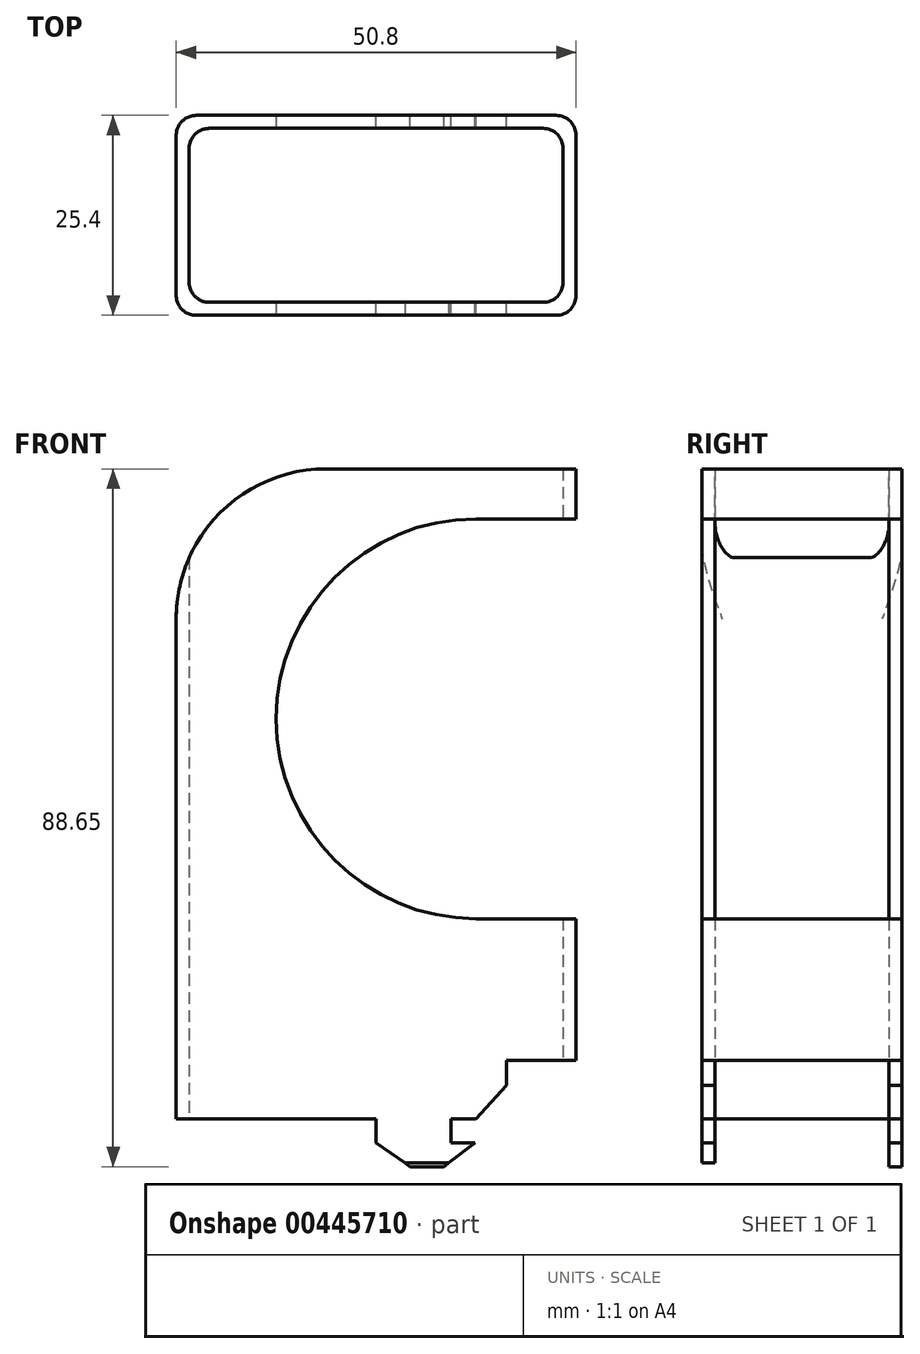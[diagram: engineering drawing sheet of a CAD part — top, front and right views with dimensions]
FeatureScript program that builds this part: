
annotation { "Feature Type Name" : "Feature", "Feature Type Description" : "" }
export const myFeature = defineFeature(function(context is Context, id is Id, definition is map)
    precondition{}
    {
        {
            var Q0;
            Q0=qCreatedBy(makeId("Top.planeOp"),FACE);
            var sketch = newSketch(context, id + "F0", { "sketchPlane" : qUnion([Q0])});
            skLineSegment(sketch, "E0.bottom", {"start": v(2.54, 0) * mm, "end": v(48.26, 0) * mm});
            skLineSegment(sketch, "E0.top", {"start": v(2.54, 25.4) * mm, "end": v(48.26, 25.4) * mm});
            skLineSegment(sketch, "E0.left", {"start": v(0, 2.54) * mm, "end": v(0, 22.86) * mm});
            skLineSegment(sketch, "E0.right", {"start": v(50.8, 2.54) * mm, "end": v(50.8, 22.86) * mm});
            skPoint(sketch, "E1.visualSharp", {"position": v(0, 25.4) * mm});
            skArc(sketch, "E1.filletArc", {"start": v(2.54, 25.4) * mm, "mid": v(0.74, 24.66) * mm, "end": v(0, 22.86) * mm});
            skPoint(sketch, "E2.visualSharp", {"position": v(50.8, 25.4) * mm});
            skArc(sketch, "E2.filletArc", {"start": v(50.8, 22.86) * mm, "mid": v(50.06, 24.66) * mm, "end": v(48.26, 25.4) * mm});
            skPoint(sketch, "E3.visualSharp", {"position": v(50.8, 0) * mm});
            skArc(sketch, "E3.filletArc", {"start": v(48.26, 0) * mm, "mid": v(50.06, 0.74) * mm, "end": v(50.8, 2.54) * mm});
            skPoint(sketch, "E4.visualSharp", {"position": v(0, 0) * mm});
            skArc(sketch, "E4.filletArc", {"start": v(0, 2.54) * mm, "mid": v(0.74, 0.74) * mm, "end": v(2.54, 0) * mm});
            skLineSegment(sketch, "E5.0", {"start": v(4.2, 23.75) * mm, "end": v(46.6, 23.75) * mm});
            skLineSegment(sketch, "E5.1", {"start": v(1.65, 4.2) * mm, "end": v(1.65, 21.2) * mm});
            skLineSegment(sketch, "E5.2", {"start": v(4.2, 1.65) * mm, "end": v(46.6, 1.65) * mm});
            skLineSegment(sketch, "E5.3", {"start": v(49.15, 4.2) * mm, "end": v(49.15, 21.2) * mm});
            skPoint(sketch, "E6.visualSharp", {"position": v(1.65, 23.75) * mm});
            skArc(sketch, "E6.filletArc", {"start": v(4.2, 23.75) * mm, "mid": v(2.4, 23) * mm, "end": v(1.65, 21.2) * mm});
            skPoint(sketch, "E7.visualSharp", {"position": v(1.65, 1.65) * mm});
            skArc(sketch, "E7.filletArc", {"start": v(1.65, 4.2) * mm, "mid": v(2.4, 2.4) * mm, "end": v(4.2, 1.65) * mm});
            skPoint(sketch, "E8.visualSharp", {"position": v(49.15, 23.75) * mm});
            skArc(sketch, "E8.filletArc", {"start": v(49.15, 21.2) * mm, "mid": v(48.4, 23) * mm, "end": v(46.6, 23.75) * mm});
            skPoint(sketch, "E9.visualSharp", {"position": v(49.15, 1.65) * mm});
            skArc(sketch, "E9.filletArc", {"start": v(46.6, 1.65) * mm, "mid": v(48.4, 2.4) * mm, "end": v(49.15, 4.2) * mm});
            skSolve(sketch);
        }
        {
            var Q0;
            Q0=makeQuery(id+"F0.imprint","IMPRINT",FACE,{"disambiguationData":[TD([[makeQuery(id+"F0.imprint","IMPRINT",EDGE,{"derivedFrom":sQuery(id+"F0.wireOp",EDGE,"E0.bottom")}),1.0]])]});
            extrude(context, id + "F1", {"entities" : qUnion([Q0]), "depth" : 82.55 * mm});
        }
        {
            var Q0;
            Q0=makeQuery(id+"F1.opExtrude","CAP_FACE",FACE,{"disambiguationData":[OSD([sQuery(id+"F0.wireOp",EDGE,"E0.bottom"),sQuery(id+"F0.wireOp",EDGE,"E0.top"),sQuery(id+"F0.wireOp",EDGE,"E0.left"),sQuery(id+"F0.wireOp",EDGE,"E0.right"),sQuery(id+"F0.wireOp",EDGE,"E1.filletArc"),sQuery(id+"F0.wireOp",EDGE,"E2.filletArc"),sQuery(id+"F0.wireOp",EDGE,"E3.filletArc"),sQuery(id+"F0.wireOp",EDGE,"E4.filletArc"),sQuery(id+"F0.wireOp",EDGE,"E5.0"),sQuery(id+"F0.wireOp",EDGE,"E5.1"),sQuery(id+"F0.wireOp",EDGE,"E5.2"),sQuery(id+"F0.wireOp",EDGE,"E5.3"),sQuery(id+"F0.wireOp",EDGE,"E6.filletArc"),sQuery(id+"F0.wireOp",EDGE,"E7.filletArc"),sQuery(id+"F0.wireOp",EDGE,"E8.filletArc"),sQuery(id+"F0.wireOp",EDGE,"E9.filletArc")])],"isStart":true});
            var sketch = newSketch(context, id + "F2", { "sketchPlane" : qUnion([Q0])});
            skLineSegment(sketch, "E10", {"start": v(34.93, 0) * mm, "end": v(34.93, -1.65) * mm});
            skLineSegment(sketch, "E11", {"start": v(25.4, 0) * mm, "end": v(25.4, -1.65) * mm});
            skLineSegment(sketch, "E12", {"start": v(34.92, -23.75) * mm, "end": v(34.92, -25.4) * mm});
            skLineSegment(sketch, "E13", {"start": v(25.4, -23.75) * mm, "end": v(25.4, -25.4) * mm});
            skSolve(sketch);
        }
        {
            var Q0;
            Q0 = qSketchRegion(id + "F2", true);
            var Q1;
            {var subQ0=sQuery(id+"F2.wireOp",EDGE,"E10");Q1=makeQuery(id+"F2.imprint","IMPRINT",FACE,{"disambiguationData":[TD([[makeQuery(id+"F2.imprint","IMPRINT",EDGE,{"derivedFrom":subQ0}),-1.0]])]});}
            var Q2;
            {var subQ0=sQuery(id+"F2.wireOp",EDGE,"E12");Q2=makeQuery(id+"F2.imprint","IMPRINT",FACE,{"disambiguationData":[TD([[makeQuery(id+"F2.imprint","IMPRINT",EDGE,{"derivedFrom":subQ0}),-1.0]])]});}
            extrude(context, id + "F3", {"entities" : qUnion([Q0, Q1, Q2]), "operationType" : NewBodyOperationType.ADD, "depth" : 12.7 * mm});
        }
        {
            var Q0;
            Q0=makeQuery(id+"F3.opExtrude","SWEPT_FACE",FACE,{"disambiguationData":[OSD([sQuery(id+"F2.wireOp",EDGE,"E10")])]});
            var sketch = newSketch(context, id + "F4", { "sketchPlane" : qUnion([Q0])});
            skLineSegment(sketch, "E14", {"start": v(0, -3.05) * mm, "end": v(1.65, -3.05) * mm});
            skSolve(sketch);
        }
        {
            var Q0;
            {var subQ0=sQuery(id+"F4.wireOp",EDGE,"E14");Q0=makeQuery(id+"F4.imprint","IMPRINT",FACE,{"disambiguationData":[TD([[makeQuery(id+"F4.imprint","IMPRINT",EDGE,{"derivedFrom":subQ0}),-1.0]])]});}
            extrude(context, id + "F5", {"entities" : qUnion([Q0]), "operationType" : NewBodyOperationType.ADD, "depth" : 3.05 * mm});
        }
        {
            var Q0;
            Q0=makeQuery(id+"F3.opExtrude","SWEPT_FACE",FACE,{"disambiguationData":[OSD([sQuery(id+"F2.wireOp",EDGE,"E12")])]});
            var sketch = newSketch(context, id + "F6", { "sketchPlane" : qUnion([Q0])});
            skLineSegment(sketch, "E15", {"start": v(23.75, -3.05) * mm, "end": v(25.4, -3.05) * mm});
            skSolve(sketch);
        }
        {
            var Q0;
            Q0 = qSketchRegion(id + "F6", true);
            var Q1;
            {var subQ0=sQuery(id+"F6.wireOp",EDGE,"E15");Q1=makeQuery(id+"F6.imprint","IMPRINT",FACE,{"disambiguationData":[TD([[makeQuery(id+"F6.imprint","IMPRINT",EDGE,{"derivedFrom":subQ0}),-1.0]])]});}
            extrude(context, id + "F7", {"entities" : qUnion([Q0, Q1]), "operationType" : NewBodyOperationType.ADD, "depth" : 3.05 * mm});
        }
        {
            var Q0;
            {var subQ0=sQuery(id+"F0.wireOp",EDGE,"E0.bottom");Q0=makeQuery(id+"F5.boolean.opBoolean","MERGE",FACE,{"derivedFrom":[makeQuery(id+"F3.boolean.opBoolean","MERGE",FACE,{"derivedFrom":[makeQuery(id+"F1.opExtrude","SWEPT_FACE",FACE,{"disambiguationData":[OSD([subQ0])]}),makeQuery(id+"F3.opExtrude","SWEPT_FACE",FACE,{"disambiguationData":[OSD([subQ0])]})]}),makeQuery(id+"F5.opExtrude","SWEPT_FACE",FACE,{"disambiguationData":[OSD([subQ0,sQuery(id+"F2.wireOp",EDGE,"E10")])]})]});}
            var sketch = newSketch(context, id + "F8", { "sketchPlane" : qUnion([Q0])});
            skLineSegment(sketch, "E16", {"start": v(37.97, -3.05) * mm, "end": v(25.4, -12.7) * mm});
            skSolve(sketch);
        }
        {
            var Q0;
            Q0 = qSketchRegion(id + "F8", true);
            var Q1;
            Q1=makeQuery(id+"F8.imprint","IMPRINT",FACE,{"disambiguationData":[TD([[makeQuery(id+"F8.imprint","IMPRINT",EDGE,{"derivedFrom":sQuery(id+"F8.wireOp",EDGE,"E16")}),1.0]])]});
            extrude(context, id + "F9", {"entities" : qUnion([Q0, Q1]), "operationType" : NewBodyOperationType.REMOVE, "oppositeDirection" : true, "depth" : 6.35 * mm});
        }
        {
            var Q0;
            {var subQ0=sQuery(id+"F0.wireOp",EDGE,"E0.top");Q0=makeQuery(id+"F7.boolean.opBoolean","MERGE",FACE,{"derivedFrom":[makeQuery(id+"F3.boolean.opBoolean","MERGE",FACE,{"derivedFrom":[makeQuery(id+"F1.opExtrude","SWEPT_FACE",FACE,{"disambiguationData":[OSD([subQ0])]}),makeQuery(id+"F3.opExtrude","SWEPT_FACE",FACE,{"disambiguationData":[OSD([subQ0])]})]}),makeQuery(id+"F7.opExtrude","SWEPT_FACE",FACE,{"disambiguationData":[OSD([subQ0,sQuery(id+"F2.wireOp",EDGE,"E12")])]})]});}
            var sketch = newSketch(context, id + "F10", { "sketchPlane" : qUnion([Q0])});
            skLineSegment(sketch, "E17", {"start": v(-37.97, -3.05) * mm, "end": v(-25.4, -12.7) * mm});
            skSolve(sketch);
        }
        {
            var Q0;
            Q0 = qSketchRegion(id + "F10", true);
            var Q1;
            Q1=makeQuery(id+"F10.imprint","IMPRINT",FACE,{"disambiguationData":[TD([[makeQuery(id+"F10.imprint","IMPRINT",EDGE,{"derivedFrom":sQuery(id+"F10.wireOp",EDGE,"E17")}),-1.0]])]});
            extrude(context, id + "F11", {"entities" : qUnion([Q0, Q1]), "operationType" : NewBodyOperationType.REMOVE, "oppositeDirection" : true, "depth" : 6.35 * mm});
        }
        {
            var Q0;
            {var subQ0=sQuery(id+"F0.wireOp",EDGE,"E0.top");Q0=makeQuery(id+"F7.boolean.opBoolean","MERGE",FACE,{"derivedFrom":[makeQuery(id+"F3.boolean.opBoolean","MERGE",FACE,{"derivedFrom":[makeQuery(id+"F1.opExtrude","SWEPT_FACE",FACE,{"disambiguationData":[OSD([subQ0])]}),makeQuery(id+"F3.opExtrude","SWEPT_FACE",FACE,{"disambiguationData":[OSD([subQ0])]})]}),makeQuery(id+"F7.opExtrude","SWEPT_FACE",FACE,{"disambiguationData":[OSD([subQ0,sQuery(id+"F2.wireOp",EDGE,"E12")])]})]});}
            var sketch = newSketch(context, id + "F12", { "sketchPlane" : qUnion([Q0])});
            skLineSegment(sketch, "E18", {"start": v(-34, -6.1) * mm, "end": v(-25.4, -6.1) * mm});
            skSolve(sketch);
        }
        {
            var Q0;
            {var subQ0=sQuery(id+"F12.wireOp",EDGE,"E18");Q0=makeQuery(id+"F12.imprint","IMPRINT",FACE,{"disambiguationData":[TD([[makeQuery(id+"F12.imprint","IMPRINT",EDGE,{"derivedFrom":subQ0}),-1.0]])]});}
            extrude(context, id + "F13", {"entities" : qUnion([Q0]), "operationType" : NewBodyOperationType.REMOVE, "oppositeDirection" : true, "depth" : 3.17 * mm});
        }
        {
            var Q0;
            {var subQ0=sQuery(id+"F0.wireOp",EDGE,"E0.bottom");Q0=makeQuery(id+"F5.boolean.opBoolean","MERGE",FACE,{"derivedFrom":[makeQuery(id+"F3.boolean.opBoolean","MERGE",FACE,{"derivedFrom":[makeQuery(id+"F1.opExtrude","SWEPT_FACE",FACE,{"disambiguationData":[OSD([subQ0])]}),makeQuery(id+"F3.opExtrude","SWEPT_FACE",FACE,{"disambiguationData":[OSD([subQ0])]})]}),makeQuery(id+"F5.opExtrude","SWEPT_FACE",FACE,{"disambiguationData":[OSD([subQ0,sQuery(id+"F2.wireOp",EDGE,"E10")])]})]});}
            var sketch = newSketch(context, id + "F14", { "sketchPlane" : qUnion([Q0])});
            skLineSegment(sketch, "E19", {"start": v(34.6, -5.64) * mm, "end": v(25.4, -5.64) * mm});
            skSolve(sketch);
        }
        {
            var Q0;
            Q0 = qSketchRegion(id + "F14", true);
            var Q1;
            {var subQ0=sQuery(id+"F14.wireOp",EDGE,"E19");Q1=makeQuery(id+"F14.imprint","IMPRINT",FACE,{"disambiguationData":[TD([[makeQuery(id+"F14.imprint","IMPRINT",EDGE,{"derivedFrom":subQ0}),1.0]])]});}
            extrude(context, id + "F15", {"entities" : qUnion([Q0, Q1]), "operationType" : NewBodyOperationType.REMOVE, "oppositeDirection" : true, "depth" : 3.17 * mm});
        }
        {
            var Q0;
            {var subQ0=sQuery(id+"F0.wireOp",EDGE,"E0.bottom");Q0=makeQuery(id+"F5.boolean.opBoolean","MERGE",FACE,{"derivedFrom":[makeQuery(id+"F3.boolean.opBoolean","MERGE",FACE,{"derivedFrom":[makeQuery(id+"F1.opExtrude","SWEPT_FACE",FACE,{"disambiguationData":[OSD([subQ0])]}),makeQuery(id+"F3.opExtrude","SWEPT_FACE",FACE,{"disambiguationData":[OSD([subQ0])]})]}),makeQuery(id+"F5.opExtrude","SWEPT_FACE",FACE,{"disambiguationData":[OSD([subQ0,sQuery(id+"F2.wireOp",EDGE,"E10")])]})]});}
            var sketch = newSketch(context, id + "F16", { "sketchPlane" : qUnion([Q0])});
            skLineSegment(sketch, "E20", {"start": v(41.94, 0) * mm, "end": v(41.94, 7.4) * mm});
            skLineSegment(sketch, "E21", {"start": v(41.94, 7.4) * mm, "end": v(50.89, 7.4) * mm});
            skLineSegment(sketch, "E22", {"start": v(50.89, 7.4) * mm, "end": v(50.89, 0) * mm});
            skLineSegment(sketch, "E23", {"start": v(50.89, 0) * mm, "end": v(41.94, 0) * mm});
            skSolve(sketch);
        }
        {
            var Q0;
            {var subQ0=sQuery(id+"F16.wireOp",EDGE,"E20");Q0=makeQuery(id+"F16.imprint","IMPRINT",FACE,{"disambiguationData":[TD([[makeQuery(id+"F16.imprint","IMPRINT",EDGE,{"derivedFrom":subQ0}),-1.0]])]});}
            var Q1;
            {var subQ0=sQuery(id+"F16.wireOp",EDGE,"E22");Q1=makeQuery(id+"F16.imprint","IMPRINT",FACE,{"disambiguationData":[TD([[makeQuery(id+"F16.imprint","IMPRINT",EDGE,{"derivedFrom":subQ0}),-1.0]])]});}
            extrude(context, id + "F17", {"entities" : qUnion([Q0, Q1]), "operationType" : NewBodyOperationType.REMOVE, "oppositeDirection" : true, "depth" : 31.75 * mm});
        }
        {
            var Q0;
            {var subQ0=sQuery(id+"F0.wireOp",EDGE,"E0.bottom");Q0=makeQuery(id+"F5.boolean.opBoolean","MERGE",FACE,{"derivedFrom":[makeQuery(id+"F3.boolean.opBoolean","MERGE",FACE,{"derivedFrom":[makeQuery(id+"F1.opExtrude","SWEPT_FACE",FACE,{"disambiguationData":[OSD([subQ0])]}),makeQuery(id+"F3.opExtrude","SWEPT_FACE",FACE,{"disambiguationData":[OSD([subQ0])]})]}),makeQuery(id+"F5.opExtrude","SWEPT_FACE",FACE,{"disambiguationData":[OSD([subQ0,sQuery(id+"F2.wireOp",EDGE,"E10")])]})]});}
            var sketch = newSketch(context, id + "F18", { "sketchPlane" : qUnion([Q0])});
            skLineSegment(sketch, "E24", {"start": v(50.8, 25.4) * mm, "end": v(50.8, 76.2) * mm});
            skLineSegment(sketch, "E25", {"start": v(50.8, 76.2) * mm, "end": v(38.1, 76.2) * mm});
            skLineSegment(sketch, "E26", {"start": v(12.7, 50.8) * mm, "end": v(12.7, 50.8) * mm});
            skLineSegment(sketch, "E27", {"start": v(50.8, 25.4) * mm, "end": v(38.1, 25.4) * mm});
            skPoint(sketch, "E28.visualSharp", {"position": v(12.7, 76.2) * mm});
            skArc(sketch, "E28.filletArc", {"start": v(38.1, 76.2) * mm, "mid": v(20.14, 68.76) * mm, "end": v(12.7, 50.8) * mm});
            skPoint(sketch, "E29.visualSharp", {"position": v(12.7, 25.4) * mm});
            skArc(sketch, "E29.filletArc", {"start": v(12.7, 50.8) * mm, "mid": v(20.14, 32.84) * mm, "end": v(38.1, 25.4) * mm});
            skSolve(sketch);
        }
        {
            var Q0;
            {var subQ1=sQuery(id+"F18.wireOp",EDGE,"E28.filletArc");Q0=makeQuery(id+"F18.imprint","IMPRINT",FACE,{"disambiguationData":[TD([[makeQuery(id+"F18.imprint","IMPRINT",EDGE,{"derivedFrom":subQ1}),1.0]])]});}
            var Q1;
            {var subQ0=sQuery(id+"F18.wireOp",EDGE,"E24");Q1=makeQuery(id+"F18.imprint","IMPRINT",FACE,{"disambiguationData":[TD([[makeQuery(id+"F18.imprint","IMPRINT",EDGE,{"derivedFrom":subQ0}),1.0]])]});}
            extrude(context, id + "F19", {"entities" : qUnion([Q0, Q1]), "operationType" : NewBodyOperationType.REMOVE, "oppositeDirection" : true, "depth" : 27.94 * mm});
        }
        {
            var Q0;
            {var subQ0=sQuery(id+"F0.wireOp",EDGE,"E0.top");Q0=makeQuery(id+"F7.boolean.opBoolean","MERGE",FACE,{"derivedFrom":[makeQuery(id+"F3.boolean.opBoolean","MERGE",FACE,{"derivedFrom":[makeQuery(id+"F1.opExtrude","SWEPT_FACE",FACE,{"disambiguationData":[OSD([subQ0])]}),makeQuery(id+"F3.opExtrude","SWEPT_FACE",FACE,{"disambiguationData":[OSD([subQ0])]})]}),makeQuery(id+"F7.opExtrude","SWEPT_FACE",FACE,{"disambiguationData":[OSD([subQ0,sQuery(id+"F2.wireOp",EDGE,"E12")])]})]});}
            var sketch = newSketch(context, id + "F20", { "sketchPlane" : qUnion([Q0])});
            skLineSegment(sketch, "E30", {"start": v(-38.1, 0) * mm, "end": v(-41.94, 4.22) * mm});
            skLineSegment(sketch, "E31", {"start": v(-29.7, -6.1) * mm, "end": v(-25.4, -3.05) * mm});
            skSolve(sketch);
        }
        {
            var Q0;
            {var subQ0=sQuery(id+"F20.wireOp",EDGE,"E31");Q0=makeQuery(id+"F20.imprint","IMPRINT",FACE,{"disambiguationData":[TD([[makeQuery(id+"F20.imprint","IMPRINT",EDGE,{"derivedFrom":subQ0}),-1.0]])]});}
            var Q1;
            {var subQ0=sQuery(id+"F20.wireOp",EDGE,"E30");Q1=makeQuery(id+"F20.imprint","IMPRINT",FACE,{"disambiguationData":[TD([[makeQuery(id+"F20.imprint","IMPRINT",EDGE,{"derivedFrom":subQ0}),1.0]])]});}
            extrude(context, id + "F21", {"entities" : qUnion([Q0, Q1]), "operationType" : NewBodyOperationType.REMOVE, "oppositeDirection" : true, "depth" : 25.4 * mm});
        }
        {
            var Q0;
            {var subQ0=sQuery(id+"F0.wireOp",EDGE,"E0.top");Q0=makeQuery(id+"F7.boolean.opBoolean","MERGE",FACE,{"derivedFrom":[makeQuery(id+"F3.boolean.opBoolean","MERGE",FACE,{"derivedFrom":[makeQuery(id+"F1.opExtrude","SWEPT_FACE",FACE,{"disambiguationData":[OSD([subQ0])]}),makeQuery(id+"F3.opExtrude","SWEPT_FACE",FACE,{"disambiguationData":[OSD([subQ0])]})]}),makeQuery(id+"F7.opExtrude","SWEPT_FACE",FACE,{"disambiguationData":[OSD([subQ0,sQuery(id+"F2.wireOp",EDGE,"E12")])]})]});}
            var sketch = newSketch(context, id + "F22", { "sketchPlane" : qUnion([Q0])});
            skLineSegment(sketch, "E32", {"start": v(-48.26, 82.55) * mm, "end": v(-19.05, 82.55) * mm});
            skPoint(sketch, "E33.visualSharp", {"position": v(0, 82.55) * mm});
            skArc(sketch, "E33.filletArc", {"start": v(0, 63.5) * mm, "mid": v(-5.58, 76.97) * mm, "end": v(-19.05, 82.55) * mm});
            skLineSegment(sketch, "E34", {"start": v(0, 63.5) * mm, "end": v(0, 82.55) * mm});
            skLineSegment(sketch, "E35", {"start": v(-19.05, 82.55) * mm, "end": v(0, 82.55) * mm});
            skSolve(sketch);
        }
        {
            var Q0;
            Q0 = qSketchRegion(id + "F22", true);
            extrude(context, id + "F23", {"entities" : qUnion([Q0]), "operationType" : NewBodyOperationType.REMOVE, "oppositeDirection" : true, "depth" : 25.4 * mm});
        }
    });
